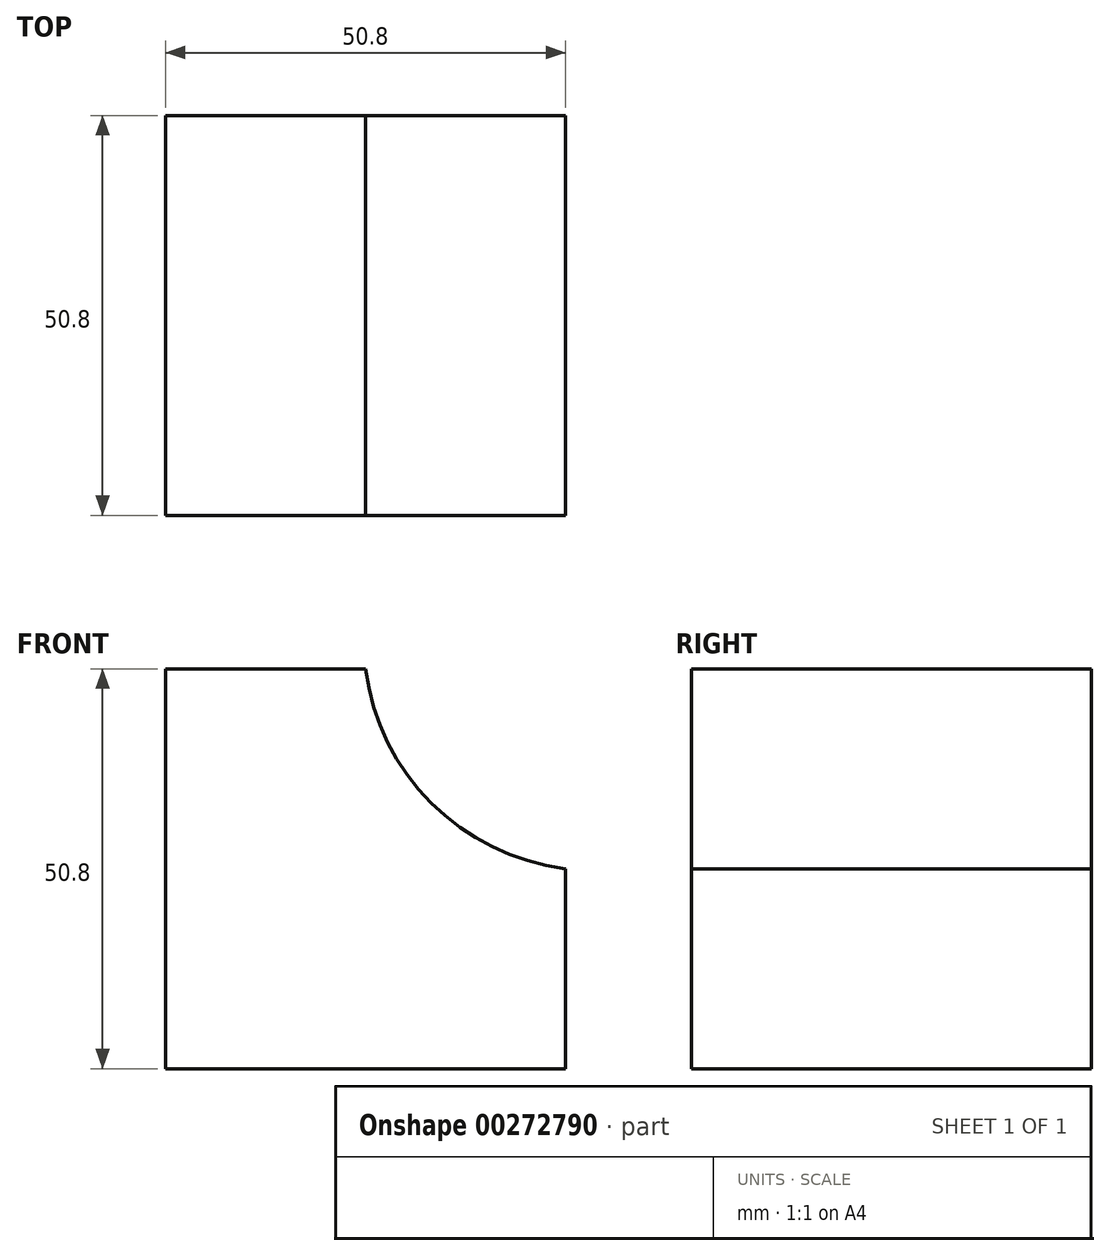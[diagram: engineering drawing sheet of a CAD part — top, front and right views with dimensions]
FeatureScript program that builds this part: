
annotation { "Feature Type Name" : "Feature", "Feature Type Description" : "" }
export const myFeature = defineFeature(function(context is Context, id is Id, definition is map)
    precondition{}
    {
        {
            var Q0;
            Q0=qCreatedBy(makeId("Front.planeOp"),FACE);
            var sketch = newSketch(context, id + "F0", { "sketchPlane" : qUnion([Q0])});
            skLineSegment(sketch, "E0", {"start": v(0, 0) * mm, "end": v(-50.8, 0) * mm});
            skPoint(sketch, "E1.end.orphan", {"position": v(-50.8, 48.42) * mm});
            skLineSegment(sketch, "E2", {"start": v(-50.8, 0) * mm, "end": v(-50.8, 50.8) * mm});
            skLineSegment(sketch, "E3", {"start": v(-50.8, 50.8) * mm, "end": v(-25.4, 50.8) * mm});
            skLineSegment(sketch, "E4", {"start": v(0, 25.4) * mm, "end": v(0, 0) * mm});
            skArc(sketch, "E5", {"start": v(-25.4, 50.8) * mm, "mid": v(-17.05, 33.75) * mm, "end": v(0, 25.4) * mm});
            skSolve(sketch);
        }
        {
            var Q0;
            Q0 = qSketchRegion(id + "F0", true);
            extrude(context, id + "F1", {"entities" : qUnion([Q0]), "depth" : 50.8 * mm});
        }
    });
